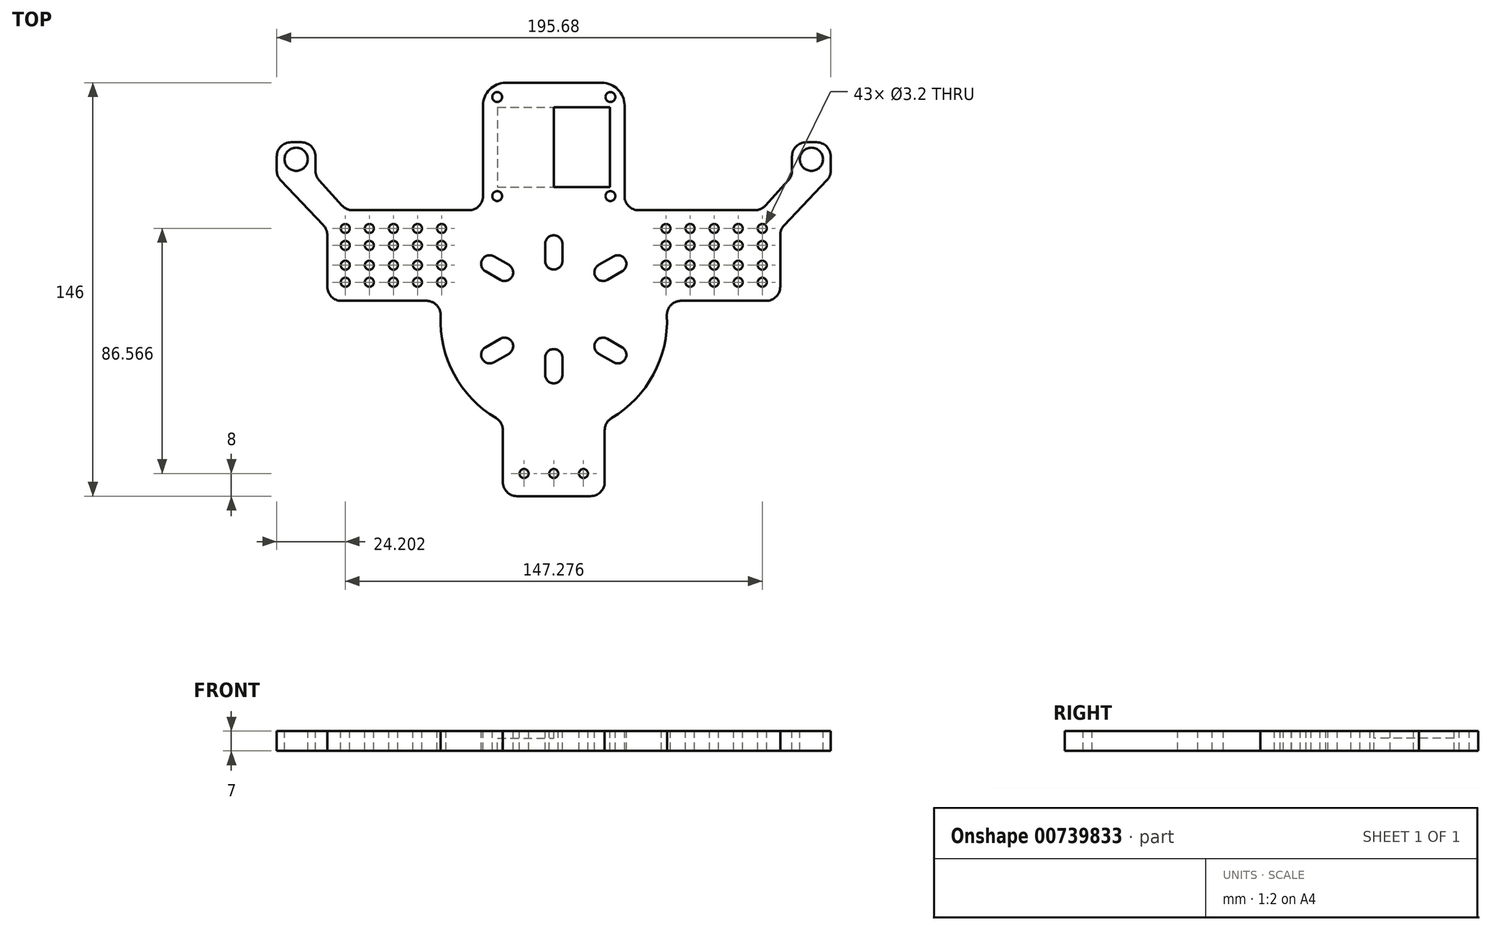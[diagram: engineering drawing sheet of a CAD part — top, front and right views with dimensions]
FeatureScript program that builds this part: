
annotation { "Feature Type Name" : "Feature", "Feature Type Description" : "" }
export const myFeature = defineFeature(function(context is Context, id is Id, definition is map)
    precondition{}
    {
        {
            var Q0;
            Q0=qCreatedBy(makeId("Top.planeOp"),FACE);
            var sketch = newSketch(context, id + "F0", { "sketchPlane" : qUnion([Q0])});
            skLineSegment(sketch, "E0.right", {"start": v(-80, 6) * mm, "end": v(-39.38, 6) * mm});
            skLineSegment(sketch, "E1.right", {"start": v(-18, -63) * mm, "end": v(0, -63) * mm});
            skPoint(sketch, "E2", {"position": v(-10.5, -55) * mm});
            skPoint(sketch, "E3", {"position": v(0, -55) * mm});
            skLineSegment(sketch, "E4", {"start": v(-73.25, 38) * mm, "end": v(-25, 38) * mm});
            skLineSegment(sketch, "E5", {"start": v(-18, -63) * mm, "end": v(-18, -36.72) * mm});
            skArc(sketch, "E6.MirrorCS", {"start": v(-39.38, 6) * mm, "mid": v(-35.77, -18.9) * mm, "end": v(-18, -36.72) * mm});
            skLineSegment(sketch, "E7", {"start": v(-80, 31.25) * mm, "end": v(-80, 6) * mm});
            skCircle(sketch, "E8", {"center": v(0, 0) * mm, "radius": 23.1 * mm, "construction": true});
            skLineSegment(sketch, "E9", {"start": v(0, 68.14) * mm, "end": v(0, -69.58) * mm, "construction": true});
            skCircle(sketch, "E10", {"center": v(0, -55) * mm, "radius": 1.6 * mm});
            skCircle(sketch, "E11", {"center": v(-10.5, -55) * mm, "radius": 1.6 * mm});
            skCircle(sketch, "E12", {"center": v(-73.64, 31.57) * mm, "radius": 1.6 * mm});
            skCircle(sketch, "E13", {"center": v(-73.64, 25.57) * mm, "radius": 1.6 * mm});
            skCircle(sketch, "E14.0.1.0", {"center": v(-73.64, 18.57) * mm, "radius": 1.6 * mm});
            skCircle(sketch, "E14.0.1.1", {"center": v(-73.64, 12.57) * mm, "radius": 1.6 * mm});
            skCircle(sketch, "E14.1.0.0", {"center": v(-65.14, 31.57) * mm, "radius": 1.6 * mm});
            skCircle(sketch, "E14.1.0.1", {"center": v(-65.14, 25.57) * mm, "radius": 1.6 * mm});
            skCircle(sketch, "E14.1.1.0", {"center": v(-65.14, 18.57) * mm, "radius": 1.6 * mm});
            skCircle(sketch, "E14.1.1.1", {"center": v(-65.14, 12.57) * mm, "radius": 1.6 * mm});
            skCircle(sketch, "E14.2.0.0", {"center": v(-56.64, 31.57) * mm, "radius": 1.6 * mm});
            skCircle(sketch, "E14.2.0.1", {"center": v(-56.64, 25.57) * mm, "radius": 1.6 * mm});
            skCircle(sketch, "E14.2.1.0", {"center": v(-56.64, 18.57) * mm, "radius": 1.6 * mm});
            skCircle(sketch, "E14.2.1.1", {"center": v(-56.64, 12.57) * mm, "radius": 1.6 * mm});
            skCircle(sketch, "E14.3.0.0", {"center": v(-48.14, 31.57) * mm, "radius": 1.6 * mm});
            skCircle(sketch, "E14.3.0.1", {"center": v(-48.14, 25.57) * mm, "radius": 1.6 * mm});
            skCircle(sketch, "E14.3.1.0", {"center": v(-48.14, 18.57) * mm, "radius": 1.6 * mm});
            skCircle(sketch, "E14.3.1.1", {"center": v(-48.14, 12.57) * mm, "radius": 1.6 * mm});
            skCircle(sketch, "E14.4.0.0", {"center": v(-39.64, 31.57) * mm, "radius": 1.6 * mm});
            skCircle(sketch, "E14.4.0.1", {"center": v(-39.64, 25.57) * mm, "radius": 1.6 * mm});
            skCircle(sketch, "E14.4.1.0", {"center": v(-39.64, 18.57) * mm, "radius": 1.6 * mm});
            skCircle(sketch, "E14.4.1.1", {"center": v(-39.64, 12.57) * mm, "radius": 1.6 * mm});
            skLineSegment(sketch, "E14.direction1", {"start": v(-73.64, 31.57) * mm, "end": v(-65.14, 31.57) * mm, "construction": true});
            skLineSegment(sketch, "E14.direction2", {"start": v(-73.64, 31.57) * mm, "end": v(-73.64, 18.57) * mm, "construction": true});
            skPoint(sketch, "E15", {"position": v(0, 23.1) * mm});
            skLineSegment(sketch, "E16", {"start": v(-20, -11.55) * mm, "end": v(20, -11.55) * mm, "construction": true});
            skLineSegment(sketch, "E17", {"start": v(0, 23.1) * mm, "end": v(-20, -11.55) * mm, "construction": true});
            skLineSegment(sketch, "E18", {"start": v(0, 23.1) * mm, "end": v(20, -11.55) * mm, "construction": true});
            skLineSegment(sketch, "E19", {"start": v(-25, 3) * mm, "end": v(25, 3) * mm, "construction": true});
            skPoint(sketch, "E20", {"position": v(0, 3) * mm});
            skPoint(sketch, "E21.MirrorP", {"position": v(0, -17.1) * mm});
            skLineSegment(sketch, "E22", {"start": v(0, 38) * mm, "end": v(0, -63) * mm});
            skArc(sketch, "E23.trimOffspring", {"start": v(3.05, 26.1) * mm, "mid": v(0, 29.14) * mm, "end": v(-3.05, 26.1) * mm});
            skLineSegment(sketch, "E24", {"start": v(-3.05, 26.1) * mm, "end": v(-3.05, 20.1) * mm});
            skArc(sketch, "E25", {"start": v(-3.05, 20.1) * mm, "mid": v(0, 17.04) * mm, "end": v(3.05, 20.1) * mm});
            skLineSegment(sketch, "E26", {"start": v(3.05, 26.1) * mm, "end": v(3.05, 20.1) * mm});
            skPoint(sketch, "E27", {"position": v(0, -11.55) * mm});
            skLineSegment(sketch, "E28", {"start": v(-3.05, 23.1) * mm, "end": v(3.05, 23.1) * mm, "construction": true});
            skArc(sketch, "E29.1.0", {"start": v(-24.12, -10.4) * mm, "mid": v(-25.24, -14.57) * mm, "end": v(-21.07, -15.69) * mm});
            skLineSegment(sketch, "E29.1.1", {"start": v(-21.07, -15.69) * mm, "end": v(-15.88, -12.69) * mm});
            skLineSegment(sketch, "E29.1.2", {"start": v(-24.12, -10.4) * mm, "end": v(-18.93, -7.4) * mm});
            skArc(sketch, "E29.1.3", {"start": v(-15.88, -12.69) * mm, "mid": v(-14.76, -8.52) * mm, "end": v(-18.93, -7.4) * mm});
            skArc(sketch, "E29.2.0", {"start": v(21.07, -15.69) * mm, "mid": v(25.24, -14.57) * mm, "end": v(24.12, -10.4) * mm});
            skLineSegment(sketch, "E29.2.1", {"start": v(24.12, -10.4) * mm, "end": v(18.93, -7.4) * mm});
            skLineSegment(sketch, "E29.2.2", {"start": v(21.07, -15.69) * mm, "end": v(15.88, -12.69) * mm});
            skArc(sketch, "E29.2.3", {"start": v(18.93, -7.4) * mm, "mid": v(14.76, -8.52) * mm, "end": v(15.88, -12.69) * mm});
            skArc(sketch, "E30.MirrorCS", {"start": v(21.07, 21.69) * mm, "mid": v(25.24, 20.57) * mm, "end": v(24.12, 16.4) * mm});
            skLineSegment(sketch, "E31.MirrorCS", {"start": v(24.12, 16.4) * mm, "end": v(18.93, 13.4) * mm});
            skArc(sketch, "E32.MirrorCS", {"start": v(18.93, 13.4) * mm, "mid": v(14.76, 14.52) * mm, "end": v(15.88, 18.69) * mm});
            skLineSegment(sketch, "E33.MirrorCS", {"start": v(21.07, 21.69) * mm, "end": v(15.88, 18.69) * mm});
            skArc(sketch, "E34.MirrorCS", {"start": v(-24.12, 16.4) * mm, "mid": v(-25.24, 20.57) * mm, "end": v(-21.07, 21.69) * mm});
            skLineSegment(sketch, "E35.MirrorCS", {"start": v(-24.12, 16.4) * mm, "end": v(-18.93, 13.4) * mm});
            skArc(sketch, "E36.MirrorCS", {"start": v(-15.88, 18.69) * mm, "mid": v(-14.76, 14.52) * mm, "end": v(-18.93, 13.4) * mm});
            skLineSegment(sketch, "E37.MirrorCS", {"start": v(-21.07, 21.69) * mm, "end": v(-15.88, 18.69) * mm});
            skArc(sketch, "E38.MirrorCS", {"start": v(3.05, -20.1) * mm, "mid": v(0, -23.14) * mm, "end": v(-3.05, -20.1) * mm});
            skLineSegment(sketch, "E39.MirrorCS", {"start": v(-3.05, -20.1) * mm, "end": v(-3.05, -14.1) * mm});
            skLineSegment(sketch, "E40.MirrorCS", {"start": v(3.05, -20.1) * mm, "end": v(3.05, -14.1) * mm});
            skArc(sketch, "E41.MirrorCS", {"start": v(-3.05, -14.1) * mm, "mid": v(0, -11.04) * mm, "end": v(3.05, -14.1) * mm});
            skCircle(sketch, "E42", {"center": v(0, 6) * mm, "radius": 23.1 * mm, "construction": true});
            skLineSegment(sketch, "E43", {"start": v(-97.84, 50) * mm, "end": v(-97.84, 62) * mm});
            skLineSegment(sketch, "E44", {"start": v(-97.84, 62) * mm, "end": v(-84.16, 62) * mm});
            skLineSegment(sketch, "E45", {"start": v(-84.16, 62) * mm, "end": v(-84.16, 50) * mm});
            skLineSegment(sketch, "E46", {"start": v(-97.84, 62) * mm, "end": v(-84.16, 50) * mm, "construction": true});
            skLineSegment(sketch, "E47", {"start": v(-97.84, 50) * mm, "end": v(-80, 31.25) * mm});
            skLineSegment(sketch, "E48", {"start": v(-84.16, 50) * mm, "end": v(-73.25, 38) * mm});
            skLineSegment(sketch, "E49", {"start": v(-97.84, 50) * mm, "end": v(-84.16, 62) * mm, "construction": true});
            skCircle(sketch, "E50", {"center": v(-91, 56) * mm, "radius": 4.1 * mm});
            skLineSegment(sketch, "E51.top", {"start": v(-25, 83) * mm, "end": v(0, 83) * mm});
            skLineSegment(sketch, "E51.left", {"start": v(-25, 38) * mm, "end": v(-25, 83) * mm});
            skLineSegment(sketch, "E51.right", {"start": v(0, 38) * mm, "end": v(0, 83) * mm});
            skPoint(sketch, "E52.orphan", {"position": v(-80, 38) * mm});
            skCircle(sketch, "E53", {"center": v(-20, 78) * mm, "radius": 1.75 * mm});
            skCircle(sketch, "E54", {"center": v(-20, 43) * mm, "radius": 1.75 * mm});
            skLineSegment(sketch, "E55.bottom", {"start": v(-19.9, 74.44) * mm, "end": v(0, 74.44) * mm});
            skLineSegment(sketch, "E55.top", {"start": v(-19.9, 46.19) * mm, "end": v(0, 46.19) * mm});
            skLineSegment(sketch, "E55.left", {"start": v(-19.9, 74.44) * mm, "end": v(-19.9, 46.19) * mm});
            skLineSegment(sketch, "E55.right", {"start": v(0, 74.44) * mm, "end": v(0, 46.19) * mm});
            skLineSegment(sketch, "E56.MirrorCS", {"start": v(19.9, 46.19) * mm, "end": v(0, 46.19) * mm});
            skLineSegment(sketch, "E57.MirrorCS", {"start": v(19.9, 74.44) * mm, "end": v(0, 74.44) * mm});
            skLineSegment(sketch, "E58.MirrorCS", {"start": v(19.9, 74.44) * mm, "end": v(19.9, 46.19) * mm});
            skSolve(sketch);
        }
        {
            var Q0;
            {var subQ0=sQuery(id+"F0.wireOp",EDGE,"JASyUUK0-iPwE-0CFG-Sq16-hXaXJr2W2aDv");var subQ1=sQuery(id+"F0.wireOp",EDGE,"E4");var subQ2=makeQuery(id+"F0.imprint","INTERSECT",VERTEX,{"derivedFrom":[subQ1,subQ0]});Q0=makeQuery(id+"F0.imprint","IMPRINT",FACE,{"disambiguationData":[TD([[makeQuery(id+"F0.imprint","IMPRINT",EDGE,{"disambiguationData":[TD([[subQ2,-1.0]])],"derivedFrom":subQ1}),-1.0]])]});}
            var Q1;
            Q1=makeQuery(id+"F0.imprint","IMPRINT",FACE,{"disambiguationData":[TD([[makeQuery(id+"F0.imprint","IMPRINT",EDGE,{"derivedFrom":sQuery(id+"F0.wireOp",EDGE,"E0.right")}),1.0]])]});
            var Q2;
            {var subQ0=sQuery(id+"F0.wireOp",EDGE,"XCy44rE4-g0ia-aiSd-ywla-jW98i2MYikTs");Q2=makeQuery(id+"F0.imprint","IMPRINT",FACE,{"disambiguationData":[TD([[makeQuery(id+"F0.imprint","IMPRINT",EDGE,{"derivedFrom":subQ0}),-1.0]])]});}
            var Q3;
            Q3=makeQuery(id+"F0.imprint","IMPRINT",FACE,{"disambiguationData":[TD([[makeQuery(id+"F0.imprint","IMPRINT",EDGE,{"derivedFrom":sQuery(id+"F0.wireOp",EDGE,"E43")}),-1.0]])]});
            var Q4;
            Q4=makeQuery(id+"F0.imprint","IMPRINT",FACE,{"disambiguationData":[TD([[makeQuery(id+"F0.imprint","IMPRINT",EDGE,{"derivedFrom":sQuery(id+"F0.wireOp",EDGE,"E51.bottom")}),1.0]])]});
            extrude(context, id + "F1", {"entities" : qUnion([Q0, Q1, Q2, Q3, Q4]), "oppositeDirection" : true, "depth" : 7 * mm, "offsetDistance" : 25.4 * mm});
        }
        {
            var Q0;
            Q0=makeQuery(id+"F1.opExtrude","SWEPT_EDGE",EDGE,{"disambiguationData":[OSD([sQuery(id+"F0.wireOp",EDGE,"E0.right"),sQuery(id+"F0.wireOp",EDGE,"E6.MirrorCS")])]});
            var Q1;
            Q1=makeQuery(id+"F1.opExtrude","SWEPT_EDGE",EDGE,{"disambiguationData":[OSD([sQuery(id+"F0.wireOp",EDGE,"E0.right"),sQuery(id+"F0.wireOp",EDGE,"E7")])]});
            var Q2;
            Q2=makeQuery(id+"F1.opExtrude","SWEPT_EDGE",EDGE,{"disambiguationData":[OSD([sQuery(id+"F0.wireOp",EDGE,"E4"),sQuery(id+"F0.wireOp",EDGE,"E7")])]});
            var Q3;
            Q3=makeQuery(id+"F1.opExtrude","SWEPT_EDGE",EDGE,{"disambiguationData":[OSD([sQuery(id+"F0.wireOp",EDGE,"E5"),sQuery(id+"F0.wireOp",EDGE,"E6.MirrorCS")])]});
            var Q4;
            Q4=makeQuery(id+"F1.opExtrude","SWEPT_EDGE",EDGE,{"disambiguationData":[OSD([sQuery(id+"F0.wireOp",EDGE,"E1.right"),sQuery(id+"F0.wireOp",EDGE,"E5")])]});
            fillet(context, id + "F2", {"entities" : qUnion([Q0, Q1, Q2, Q3, Q4]), "radius" : 5 * mm, "tangentPropagation" : true, "allowEdgeOverflow" : false});
        }
        {
            var Q0;
            Q0=makeQuery(id+"F1.opExtrude","SWEPT_BODY",BODY,{"disambiguationData":[OSD([sQuery(id+"F0.wireOp",EDGE,"E0.right"),sQuery(id+"F0.wireOp",EDGE,"E1.right"),sQuery(id+"F0.wireOp",EDGE,"E4"),sQuery(id+"F0.wireOp",EDGE,"E5"),sQuery(id+"F0.wireOp",EDGE,"E6.MirrorCS"),sQuery(id+"F0.wireOp",EDGE,"E7"),sQuery(id+"F0.wireOp",EDGE,"E10"),sQuery(id+"F0.wireOp",EDGE,"E11"),sQuery(id+"F0.wireOp",EDGE,"E12"),sQuery(id+"F0.wireOp",EDGE,"E13"),sQuery(id+"F0.wireOp",EDGE,"E14.0.1.0"),sQuery(id+"F0.wireOp",EDGE,"E14.0.1.1"),sQuery(id+"F0.wireOp",EDGE,"E14.1.0.0"),sQuery(id+"F0.wireOp",EDGE,"E14.1.0.1"),sQuery(id+"F0.wireOp",EDGE,"E14.1.1.0"),sQuery(id+"F0.wireOp",EDGE,"E14.1.1.1"),sQuery(id+"F0.wireOp",EDGE,"E14.2.0.0"),sQuery(id+"F0.wireOp",EDGE,"E14.2.0.1"),sQuery(id+"F0.wireOp",EDGE,"E14.2.1.0"),sQuery(id+"F0.wireOp",EDGE,"E14.2.1.1"),sQuery(id+"F0.wireOp",EDGE,"E14.3.0.0"),sQuery(id+"F0.wireOp",EDGE,"E14.3.0.1"),sQuery(id+"F0.wireOp",EDGE,"E14.3.1.0"),sQuery(id+"F0.wireOp",EDGE,"E14.3.1.1"),sQuery(id+"F0.wireOp",EDGE,"E14.4.0.0"),sQuery(id+"F0.wireOp",EDGE,"E14.4.0.1"),sQuery(id+"F0.wireOp",EDGE,"E14.4.1.0"),sQuery(id+"F0.wireOp",EDGE,"E14.4.1.1"),sQuery(id+"F0.wireOp",EDGE,"VqQO1b7S-kjUe-9xQp-IYky-dqUJku1GD5b1"),sQuery(id+"F0.wireOp",EDGE,"E22"),sQuery(id+"F0.wireOp",EDGE,"E23.trimOffspring"),sQuery(id+"F0.wireOp",EDGE,"E24"),sQuery(id+"F0.wireOp",EDGE,"E25"),sQuery(id+"F0.wireOp",EDGE,"E29.1.0"),sQuery(id+"F0.wireOp",EDGE,"E29.1.1"),sQuery(id+"F0.wireOp",EDGE,"E29.1.2"),sQuery(id+"F0.wireOp",EDGE,"E29.1.3"),sQuery(id+"F0.wireOp",EDGE,"E34.MirrorCS"),sQuery(id+"F0.wireOp",EDGE,"E35.MirrorCS"),sQuery(id+"F0.wireOp",EDGE,"E36.MirrorCS"),sQuery(id+"F0.wireOp",EDGE,"E37.MirrorCS"),sQuery(id+"F0.wireOp",EDGE,"E38.MirrorCS"),sQuery(id+"F0.wireOp",EDGE,"E39.MirrorCS"),sQuery(id+"F0.wireOp",EDGE,"E41.MirrorCS")])]});
            var Q1;
            Q1=qCreatedBy(makeId("Right.planeOp"),FACE);
            mirror(context, id + "F3", {"operationType" : NewBodyOperationType.ADD, "entities" : qUnion([Q0]), "mirrorPlane" : qUnion([Q1])});
        }
        {
            var Q0;
            Q0=makeQuery(id+"F1.opExtrude","SWEPT_EDGE",EDGE,{"disambiguationData":[OSD([sQuery(id+"F0.wireOp",EDGE,"XCy44rE4-g0ia-aiSd-ywla-jW98i2MYikTs"),sQuery(id+"F0.wireOp",EDGE,"E43")])]});
            var Q1;
            Q1=makeQuery(id+"F1.opExtrude","SWEPT_EDGE",EDGE,{"disambiguationData":[OSD([sQuery(id+"F0.wireOp",EDGE,"E43"),sQuery(id+"F0.wireOp",EDGE,"E44")])]});
            var Q2;
            Q2=makeQuery(id+"F1.opExtrude","SWEPT_EDGE",EDGE,{"disambiguationData":[OSD([sQuery(id+"F0.wireOp",EDGE,"E44"),sQuery(id+"F0.wireOp",EDGE,"E45")])]});
            var Q3;
            Q3=makeQuery(id+"F1.opExtrude","SWEPT_EDGE",EDGE,{"disambiguationData":[OSD([sQuery(id+"F0.wireOp",EDGE,"E45"),sQuery(id+"F0.wireOp",EDGE,"9XVPd7WZ-hQDh-MvCe-B6Ps-pHFIXLrTIiSV")])]});
            var Q4;
            Q4=makeQuery(id+"F1.opExtrude","SWEPT_EDGE",EDGE,{"disambiguationData":[OSD([sQuery(id+"F0.wireOp",EDGE,"E4"),sQuery(id+"F0.wireOp",EDGE,"9XVPd7WZ-hQDh-MvCe-B6Ps-pHFIXLrTIiSV")])]});
            var Q5;
            Q5=makeQuery(id+"F3.opPattern","COPY",EDGE,{"derivedFrom":makeQuery(id+"F1.opExtrude","SWEPT_EDGE",EDGE,{"disambiguationData":[OSD([sQuery(id+"F0.wireOp",EDGE,"XCy44rE4-g0ia-aiSd-ywla-jW98i2MYikTs"),sQuery(id+"F0.wireOp",EDGE,"E43")])]}),"instanceName":"1"});
            var Q6;
            Q6=makeQuery(id+"F3.opPattern","COPY",EDGE,{"derivedFrom":makeQuery(id+"F1.opExtrude","SWEPT_EDGE",EDGE,{"disambiguationData":[OSD([sQuery(id+"F0.wireOp",EDGE,"E43"),sQuery(id+"F0.wireOp",EDGE,"E44")])]}),"instanceName":"1"});
            var Q7;
            Q7=makeQuery(id+"F3.opPattern","COPY",EDGE,{"derivedFrom":makeQuery(id+"F1.opExtrude","SWEPT_EDGE",EDGE,{"disambiguationData":[OSD([sQuery(id+"F0.wireOp",EDGE,"E44"),sQuery(id+"F0.wireOp",EDGE,"E45")])]}),"instanceName":"1"});
            var Q8;
            Q8=makeQuery(id+"F3.opPattern","COPY",EDGE,{"derivedFrom":makeQuery(id+"F1.opExtrude","SWEPT_EDGE",EDGE,{"disambiguationData":[OSD([sQuery(id+"F0.wireOp",EDGE,"E45"),sQuery(id+"F0.wireOp",EDGE,"9XVPd7WZ-hQDh-MvCe-B6Ps-pHFIXLrTIiSV")])]}),"instanceName":"1"});
            var Q9;
            Q9=makeQuery(id+"F3.opPattern","COPY",EDGE,{"derivedFrom":makeQuery(id+"F1.opExtrude","SWEPT_EDGE",EDGE,{"disambiguationData":[OSD([sQuery(id+"F0.wireOp",EDGE,"E4"),sQuery(id+"F0.wireOp",EDGE,"9XVPd7WZ-hQDh-MvCe-B6Ps-pHFIXLrTIiSV")])]}),"instanceName":"1"});
            fillet(context, id + "F4", {"entities" : qUnion([Q0, Q1, Q2, Q3, Q4, Q5, Q6, Q7, Q8, Q9]), "radius" : 5 * mm, "tangentPropagation" : true, "allowEdgeOverflow" : false});
        }
        {
            var Q0;
            Q0=makeQuery(id+"F1.opExtrude","SWEPT_EDGE",EDGE,{"disambiguationData":[OSD([sQuery(id+"F0.wireOp",EDGE,"E4"),sQuery(id+"F0.wireOp",EDGE,"E51.bottom"),sQuery(id+"F0.wireOp",EDGE,"E51.left")])]});
            var Q1;
            Q1=makeQuery(id+"F1.opExtrude","SWEPT_EDGE",EDGE,{"disambiguationData":[OSD([sQuery(id+"F0.wireOp",EDGE,"E51.top"),sQuery(id+"F0.wireOp",EDGE,"E51.left")])]});
            var Q2;
            Q2=makeQuery(id+"F3.opPattern","COPY",EDGE,{"derivedFrom":makeQuery(id+"F1.opExtrude","SWEPT_EDGE",EDGE,{"disambiguationData":[OSD([sQuery(id+"F0.wireOp",EDGE,"E4"),sQuery(id+"F0.wireOp",EDGE,"E51.bottom"),sQuery(id+"F0.wireOp",EDGE,"E51.left")])]}),"instanceName":"1"});
            var Q3;
            Q3=makeQuery(id+"F3.opPattern","COPY",EDGE,{"derivedFrom":makeQuery(id+"F1.opExtrude","SWEPT_EDGE",EDGE,{"disambiguationData":[OSD([sQuery(id+"F0.wireOp",EDGE,"E51.top"),sQuery(id+"F0.wireOp",EDGE,"E51.left")])]}),"instanceName":"1"});
            fillet(context, id + "F5", {"entities" : qUnion([Q0, Q1, Q2, Q3]), "radius" : 8 * mm, "tangentPropagation" : true, "allowEdgeOverflow" : false});
        }
        {
            var Q0;
            Q0=makeQuery(id+"F0.imprint","IMPRINT",FACE,{"disambiguationData":[TD([[makeQuery(id+"F0.imprint","IMPRINT",EDGE,{"derivedFrom":sQuery(id+"F0.wireOp",EDGE,"E55.bottom")}),-1.0]])]});
            var Q1;
            Q1=makeQuery(id+"F0.imprint","IMPRINT",FACE,{"disambiguationData":[TD([[makeQuery(id+"F0.imprint","IMPRINT",EDGE,{"derivedFrom":sQuery(id+"F0.wireOp",EDGE,"E55.right")}),1.0]])]});
            extrude(context, id + "F6", {"entities" : qUnion([Q0, Q1]), "operationType" : NewBodyOperationType.ADD, "oppositeDirection" : true, "depth" : 2.5 * mm, "offsetDistance" : 25 * mm});
        }
    });
